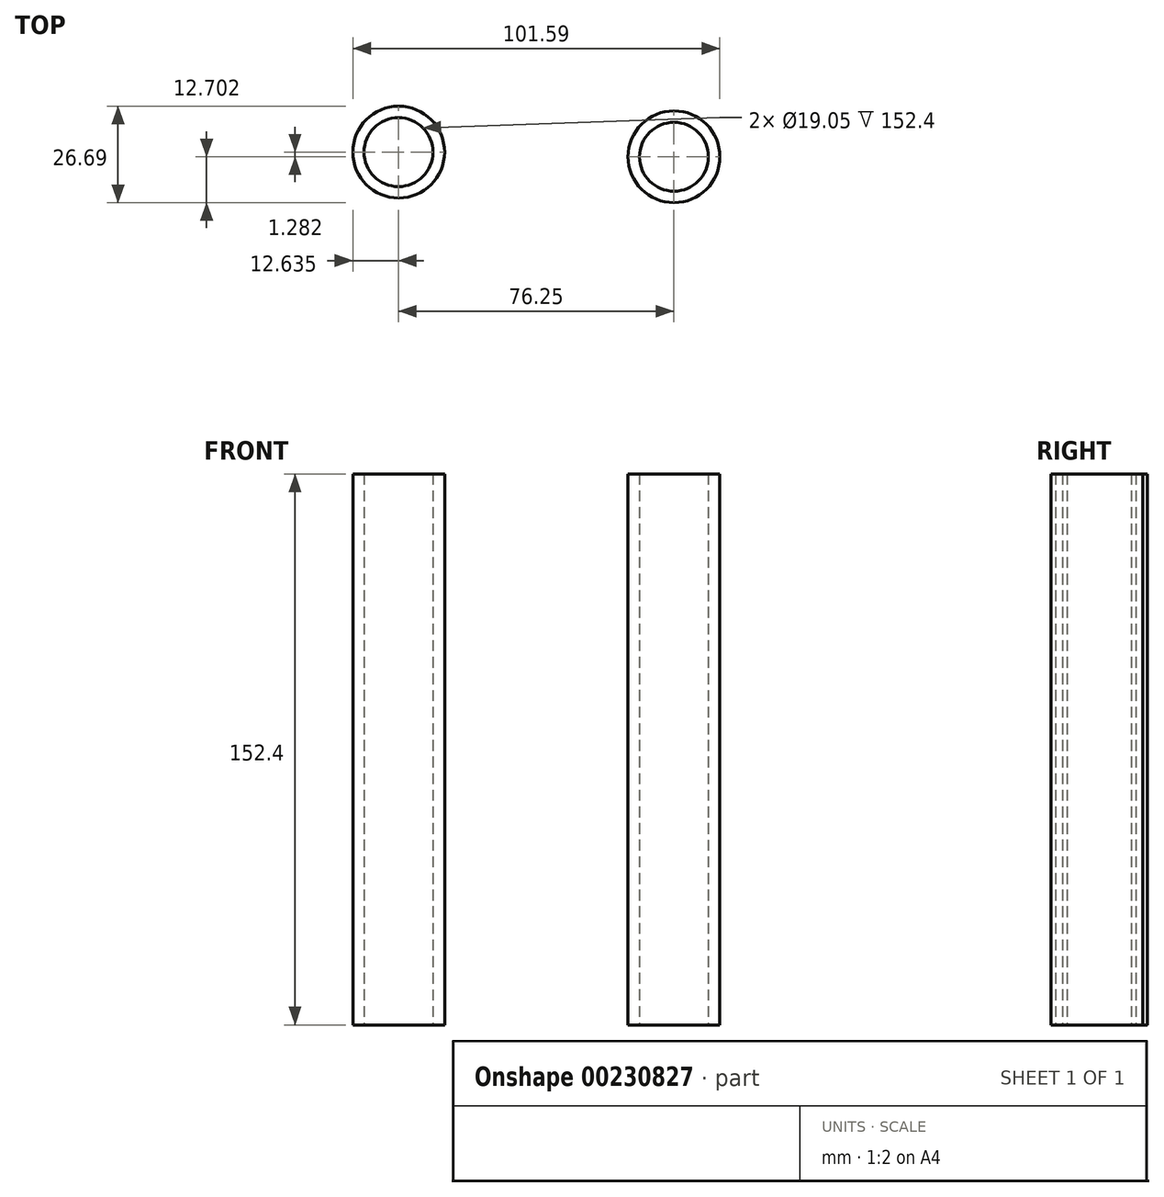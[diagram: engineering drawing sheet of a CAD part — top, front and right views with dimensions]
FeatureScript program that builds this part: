
annotation { "Feature Type Name" : "Feature", "Feature Type Description" : "" }
export const myFeature = defineFeature(function(context is Context, id is Id, definition is map)
    precondition{}
    {
        {
            var Q0;
            Q0=qCreatedBy(makeId("Top.planeOp"),FACE);
            var sketch = newSketch(context, id + "F0", { "sketchPlane" : qUnion([Q0])});
            skCircle(sketch, "E0", {"center": v(-46.83, 20.23) * mm, "radius": 12.7 * mm});
            skCircle(sketch, "E1", {"center": v(29.36, 18.94) * mm, "radius": 12.7 * mm});
            skCircle(sketch, "E2", {"center": v(-46.9, 20.22) * mm, "radius": 9.53 * mm});
            skCircle(sketch, "E3", {"center": v(29.36, 18.94) * mm, "radius": 9.53 * mm});
            skSolve(sketch);
        }
        {
            var Q0;
            Q0 = qSketchRegion(id + "F0", true);
            extrude(context, id + "F1", {"entities" : qUnion([Q0]), "depth" : 152.4 * mm});
        }
    });
